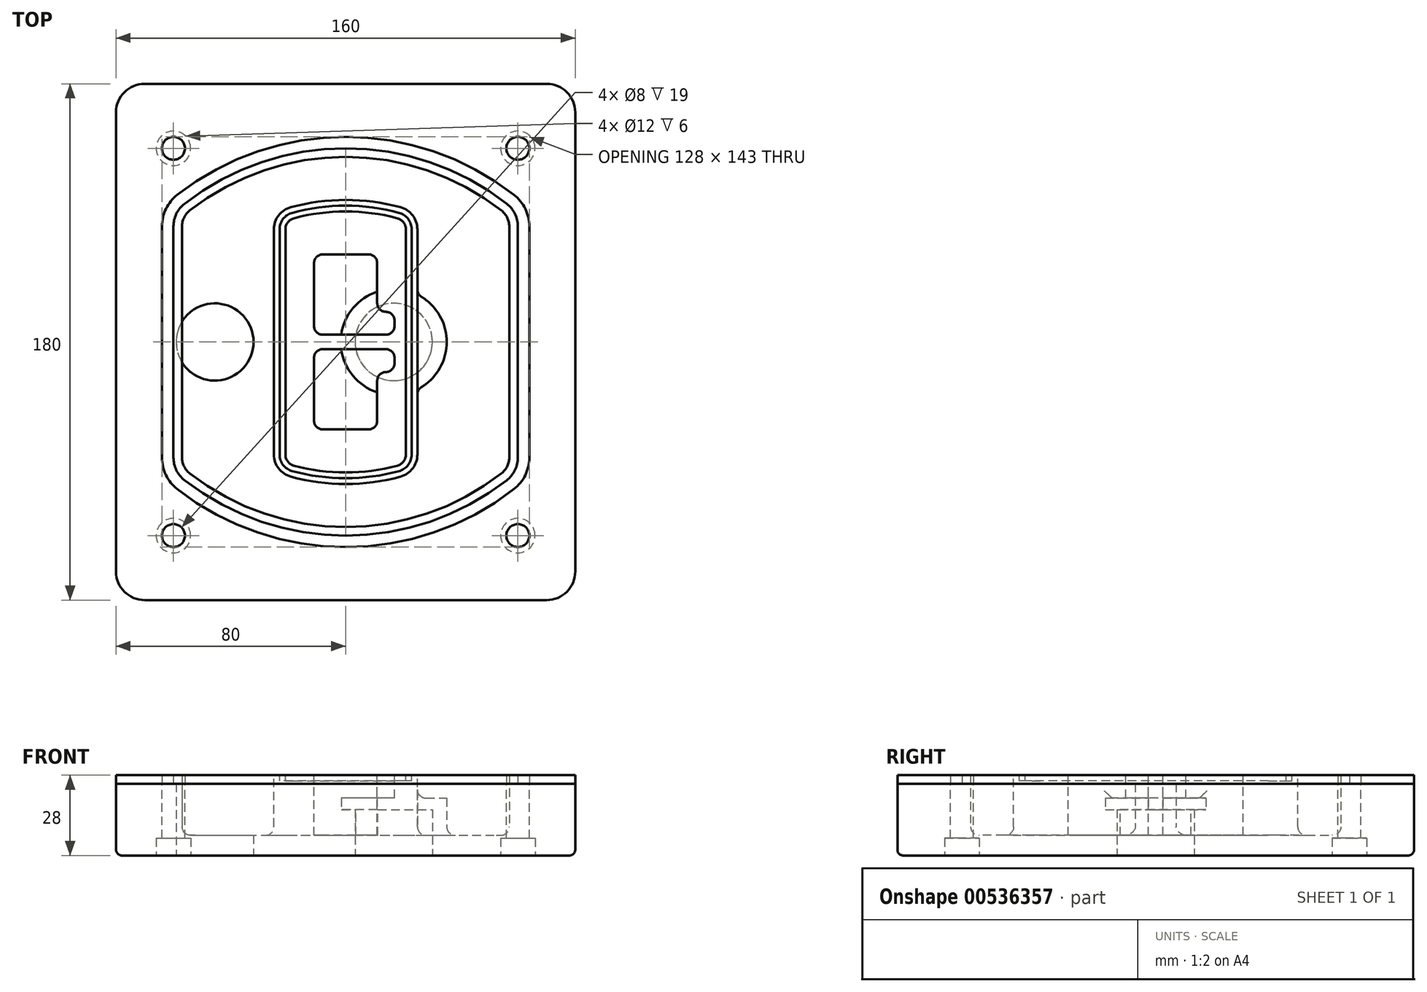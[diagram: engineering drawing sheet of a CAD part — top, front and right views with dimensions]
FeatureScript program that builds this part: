
annotation { "Feature Type Name" : "Feature", "Feature Type Description" : "" }
export const myFeature = defineFeature(function(context is Context, id is Id, definition is map)
    precondition{}
    {
        {
            var Q0;
            Q0=qCreatedBy(makeId("Top.planeOp"),FACE);
            var sketch = newSketch(context, id + "F0", { "sketchPlane" : qUnion([Q0])});
            skPoint(sketch, "E0.rect.middle", {"position": v(0, 0) * mm});
            skLineSegment(sketch, "E1.bottom", {"start": v(-70, -90) * mm, "end": v(70, -90) * mm});
            skLineSegment(sketch, "E1.top", {"start": v(-70, 90) * mm, "end": v(70, 90) * mm});
            skLineSegment(sketch, "E1.left", {"start": v(-80, -80) * mm, "end": v(-80, 80) * mm});
            skLineSegment(sketch, "E1.right", {"start": v(80, -80) * mm, "end": v(80, 80) * mm});
            skLineSegment(sketch, "E2", {"start": v(-80, 90) * mm, "end": v(80, -90) * mm, "construction": true});
            skLineSegment(sketch, "E3", {"start": v(80, 90) * mm, "end": v(-80, -90) * mm, "construction": true});
            skCircle(sketch, "E4", {"center": v(-60, 67.5) * mm, "radius": 4 * mm});
            skCircle(sketch, "E5", {"center": v(60, 67.5) * mm, "radius": 4 * mm});
            skCircle(sketch, "E6", {"center": v(60, -67.5) * mm, "radius": 4 * mm});
            skCircle(sketch, "E7", {"center": v(-60, -67.5) * mm, "radius": 4 * mm});
            skLineSegment(sketch, "E8", {"start": v(-60, 67.5) * mm, "end": v(60, 67.5) * mm, "construction": true});
            skLineSegment(sketch, "E9", {"start": v(60, 67.5) * mm, "end": v(60, -67.5) * mm, "construction": true});
            skLineSegment(sketch, "E10", {"start": v(60, -67.5) * mm, "end": v(-60, -67.5) * mm, "construction": true});
            skLineSegment(sketch, "E11", {"start": v(-60, -67.5) * mm, "end": v(-60, 67.5) * mm, "construction": true});
            skLineSegment(sketch, "E12", {"start": v(-60, 40.3) * mm, "end": v(-60, -40.3) * mm});
            skLineSegment(sketch, "E13", {"start": v(60, 40.3) * mm, "end": v(60, -40.3) * mm});
            skArc(sketch, "E14", {"start": v(56.15, 48.18) * mm, "mid": v(0, 67.5) * mm, "end": v(-56.15, 48.18) * mm});
            skArc(sketch, "E15", {"start": v(-56.15, -48.18) * mm, "mid": v(0, -67.5) * mm, "end": v(56.15, -48.18) * mm});
            skLineSegment(sketch, "E16", {"start": v(-60, 0) * mm, "end": v(60, 0) * mm, "construction": true});
            skPoint(sketch, "E17.visualSharp", {"position": v(-60, -45) * mm});
            skArc(sketch, "E17.filletArc", {"start": v(-60, -40.3) * mm, "mid": v(-58.99, -44.68) * mm, "end": v(-56.15, -48.18) * mm});
            skPoint(sketch, "E18.visualSharp", {"position": v(-60, 45) * mm});
            skArc(sketch, "E18.filletArc", {"start": v(-56.15, 48.18) * mm, "mid": v(-58.99, 44.68) * mm, "end": v(-60, 40.3) * mm});
            skPoint(sketch, "E19.visualSharp", {"position": v(60, 45) * mm});
            skArc(sketch, "E19.filletArc", {"start": v(60, 40.3) * mm, "mid": v(58.99, 44.68) * mm, "end": v(56.15, 48.18) * mm});
            skPoint(sketch, "E20.visualSharp", {"position": v(60, -45) * mm});
            skArc(sketch, "E20.filletArc", {"start": v(56.15, -48.18) * mm, "mid": v(58.99, -44.68) * mm, "end": v(60, -40.3) * mm});
            skPoint(sketch, "E21.visualSharp", {"position": v(-80, 90) * mm});
            skArc(sketch, "E21.filletArc", {"start": v(-70, 90) * mm, "mid": v(-77.07, 87.07) * mm, "end": v(-80, 80) * mm});
            skPoint(sketch, "E22.visualSharp", {"position": v(80, 90) * mm});
            skArc(sketch, "E22.filletArc", {"start": v(80, 80) * mm, "mid": v(77.07, 87.07) * mm, "end": v(70, 90) * mm});
            skPoint(sketch, "E23.visualSharp", {"position": v(80, -90) * mm});
            skArc(sketch, "E23.filletArc", {"start": v(70, -90) * mm, "mid": v(77.07, -87.07) * mm, "end": v(80, -80) * mm});
            skPoint(sketch, "E24.visualSharp", {"position": v(-80, -90) * mm});
            skArc(sketch, "E24.filletArc", {"start": v(-80, -80) * mm, "mid": v(-77.07, -87.07) * mm, "end": v(-70, -90) * mm});
            skArc(sketch, "E25.0", {"start": v(57, 40.3) * mm, "mid": v(56.3, 43.36) * mm, "end": v(54.3, 45.81) * mm});
            skLineSegment(sketch, "E25.1", {"start": v(57, 40.3) * mm, "end": v(57, -40.3) * mm});
            skArc(sketch, "E25.2", {"start": v(54.3, -45.81) * mm, "mid": v(56.3, -43.36) * mm, "end": v(57, -40.3) * mm});
            skArc(sketch, "E25.3", {"start": v(-54.3, -45.81) * mm, "mid": v(0, -64.5) * mm, "end": v(54.3, -45.81) * mm});
            skArc(sketch, "E25.4", {"start": v(-57, -40.3) * mm, "mid": v(-56.3, -43.36) * mm, "end": v(-54.3, -45.81) * mm});
            skArc(sketch, "E25.5", {"start": v(54.3, 45.81) * mm, "mid": v(0, 64.5) * mm, "end": v(-54.3, 45.81) * mm});
            skLineSegment(sketch, "E25.6", {"start": v(-57, 40.3) * mm, "end": v(-57, -40.3) * mm});
            skArc(sketch, "E25.7", {"start": v(-54.3, 45.81) * mm, "mid": v(-56.3, 43.36) * mm, "end": v(-57, 40.3) * mm});
            skArc(sketch, "E26.0", {"start": v(-58.62, 51.33) * mm, "mid": v(-62.58, 46.43) * mm, "end": v(-64, 40.3) * mm});
            skArc(sketch, "E26.1", {"start": v(58.62, 51.33) * mm, "mid": v(0, 71.5) * mm, "end": v(-58.62, 51.33) * mm});
            skArc(sketch, "E26.2", {"start": v(64, 40.3) * mm, "mid": v(62.58, 46.43) * mm, "end": v(58.62, 51.33) * mm});
            skLineSegment(sketch, "E26.3", {"start": v(64, 40.3) * mm, "end": v(64, -40.3) * mm});
            skArc(sketch, "E26.4", {"start": v(58.62, -51.33) * mm, "mid": v(62.58, -46.43) * mm, "end": v(64, -40.3) * mm});
            skLineSegment(sketch, "E26.5", {"start": v(-64, 40.3) * mm, "end": v(-64, -40.3) * mm});
            skArc(sketch, "E26.6", {"start": v(-58.62, -51.33) * mm, "mid": v(0, -71.5) * mm, "end": v(58.62, -51.33) * mm});
            skArc(sketch, "E26.7", {"start": v(-64, -40.3) * mm, "mid": v(-62.58, -46.43) * mm, "end": v(-58.62, -51.33) * mm});
            skSolve(sketch);
        }
        {
            var Q0;
            Q0=makeQuery(id+"F0.imprint","IMPRINT",FACE,{"disambiguationData":[TD([[makeQuery(id+"F0.imprint","IMPRINT",EDGE,{"derivedFrom":sQuery(id+"F0.wireOp",EDGE,"E1.bottom")}),1.0]])]});
            var Q1;
            Q1=makeQuery(id+"F0.imprint","IMPRINT",FACE,{"disambiguationData":[TD([[makeQuery(id+"F0.imprint","IMPRINT",EDGE,{"derivedFrom":sQuery(id+"F0.wireOp",EDGE,"E12")}),1.0]])]});
            var Q2;
            Q2=makeQuery(id+"F0.imprint","IMPRINT",FACE,{"disambiguationData":[TD([[makeQuery(id+"F0.imprint","IMPRINT",EDGE,{"derivedFrom":sQuery(id+"F0.wireOp",EDGE,"E25.0")}),1.0]])]});
            var Q3;
            Q3=makeQuery(id+"F0.imprint","IMPRINT",FACE,{"disambiguationData":[TD([[makeQuery(id+"F0.imprint","IMPRINT",EDGE,{"derivedFrom":sQuery(id+"F0.wireOp",EDGE,"E12")}),-1.0]])]});
            extrude(context, id + "F1", {"entities" : qUnion([Q0, Q1, Q2, Q3]), "oppositeDirection" : true, "depth" : 25 * mm});
        }
        {
            var Q0;
            Q0=makeQuery(id+"F0.imprint","IMPRINT",FACE,{"disambiguationData":[TD([[makeQuery(id+"F0.imprint","IMPRINT",EDGE,{"derivedFrom":sQuery(id+"F0.wireOp",EDGE,"E12")}),1.0]])]});
            extrude(context, id + "F2", {"entities" : qUnion([Q0]), "operationType" : NewBodyOperationType.ADD, "depth" : 3 * mm});
        }
        {
            var Q0;
            Q0=makeQuery(id+"F0.imprint","IMPRINT",FACE,{"disambiguationData":[TD([[makeQuery(id+"F0.imprint","IMPRINT",EDGE,{"derivedFrom":sQuery(id+"F0.wireOp",EDGE,"E25.0")}),1.0]])]});
            extrude(context, id + "F3", {"entities" : qUnion([Q0]), "operationType" : NewBodyOperationType.REMOVE, "oppositeDirection" : true, "depth" : 18 * mm});
        }
        {
            var Q0;
            Q0=makeQuery(id+"F2.opExtrude","CAP_FACE",FACE,{"disambiguationData":[OSD([sQuery(id+"F0.wireOp",EDGE,"E12"),sQuery(id+"F0.wireOp",EDGE,"E13"),sQuery(id+"F0.wireOp",EDGE,"E14"),sQuery(id+"F0.wireOp",EDGE,"E15"),sQuery(id+"F0.wireOp",EDGE,"E17.filletArc"),sQuery(id+"F0.wireOp",EDGE,"E18.filletArc"),sQuery(id+"F0.wireOp",EDGE,"E19.filletArc"),sQuery(id+"F0.wireOp",EDGE,"E20.filletArc"),sQuery(id+"F0.wireOp",EDGE,"E25.0"),sQuery(id+"F0.wireOp",EDGE,"E25.1"),sQuery(id+"F0.wireOp",EDGE,"E25.2"),sQuery(id+"F0.wireOp",EDGE,"E25.3"),sQuery(id+"F0.wireOp",EDGE,"E25.4"),sQuery(id+"F0.wireOp",EDGE,"E25.5"),sQuery(id+"F0.wireOp",EDGE,"E25.6"),sQuery(id+"F0.wireOp",EDGE,"E25.7")])],"isStart":false});
            var sketch = newSketch(context, id + "F4", { "sketchPlane" : qUnion([Q0])});
            skArc(sketch, "E27.0", {"start": v(-19.08, -46.97) * mm, "mid": v(0, -49.5) * mm, "end": v(19.08, -46.97) * mm});
            skArc(sketch, "E28.0", {"start": v(19.08, 46.97) * mm, "mid": v(0, 49.5) * mm, "end": v(-19.08, 46.97) * mm});
            skLineSegment(sketch, "E29", {"start": v(-25, 39.25) * mm, "end": v(-25, -39.25) * mm});
            skLineSegment(sketch, "E30", {"start": v(25, 39.25) * mm, "end": v(25, -39.25) * mm});
            skLineSegment(sketch, "E31", {"start": v(-25, 45.1) * mm, "end": v(25, 45.1) * mm, "construction": true});
            skLineSegment(sketch, "E32", {"start": v(-25, -45.1) * mm, "end": v(25, -45.1) * mm, "construction": true});
            skPoint(sketch, "E33.visualSharp", {"position": v(-25, 45.1) * mm});
            skArc(sketch, "E33.filletArc", {"start": v(-19.08, 46.97) * mm, "mid": v(-23.35, 44.11) * mm, "end": v(-25, 39.25) * mm});
            skPoint(sketch, "E34.visualSharp", {"position": v(25, 45.1) * mm});
            skArc(sketch, "E34.filletArc", {"start": v(25, 39.25) * mm, "mid": v(23.35, 44.11) * mm, "end": v(19.08, 46.97) * mm});
            skPoint(sketch, "E35.visualSharp", {"position": v(25, -45.1) * mm});
            skArc(sketch, "E35.filletArc", {"start": v(19.08, -46.97) * mm, "mid": v(23.35, -44.11) * mm, "end": v(25, -39.25) * mm});
            skPoint(sketch, "E36.visualSharp", {"position": v(-25, -45.1) * mm});
            skArc(sketch, "E36.filletArc", {"start": v(-25, -39.25) * mm, "mid": v(-23.35, -44.11) * mm, "end": v(-19.08, -46.97) * mm});
            skArc(sketch, "E37.0", {"start": v(54.3, 45.81) * mm, "mid": v(0, 64.5) * mm, "end": v(-54.3, 45.81) * mm});
            skArc(sketch, "E37.1", {"start": v(-54.3, 45.81) * mm, "mid": v(-56.3, 43.36) * mm, "end": v(-57, 40.3) * mm});
            skLineSegment(sketch, "E37.2", {"start": v(-57, 40.3) * mm, "end": v(-57, -40.3) * mm});
            skArc(sketch, "E37.3", {"start": v(-57, -40.3) * mm, "mid": v(-56.3, -43.36) * mm, "end": v(-54.3, -45.81) * mm});
            skArc(sketch, "E37.4", {"start": v(-54.3, -45.81) * mm, "mid": v(0, -64.5) * mm, "end": v(54.3, -45.81) * mm});
            skArc(sketch, "E37.5", {"start": v(54.3, -45.81) * mm, "mid": v(56.3, -43.36) * mm, "end": v(57, -40.3) * mm});
            skLineSegment(sketch, "E37.6", {"start": v(57, 40.3) * mm, "end": v(57, -40.3) * mm});
            skArc(sketch, "E37.7", {"start": v(57, 40.3) * mm, "mid": v(56.3, 43.36) * mm, "end": v(54.3, 45.81) * mm});
            skLineSegment(sketch, "E38.0", {"start": v(23, 39.25) * mm, "end": v(23, -39.25) * mm});
            skArc(sketch, "E38.1", {"start": v(18.56, -45.04) * mm, "mid": v(21.76, -42.9) * mm, "end": v(23, -39.25) * mm});
            skArc(sketch, "E38.2", {"start": v(-18.56, -45.04) * mm, "mid": v(0, -47.5) * mm, "end": v(18.56, -45.04) * mm});
            skArc(sketch, "E38.3", {"start": v(-23, -39.25) * mm, "mid": v(-21.76, -42.9) * mm, "end": v(-18.56, -45.04) * mm});
            skLineSegment(sketch, "E38.4", {"start": v(-23, 39.25) * mm, "end": v(-23, -39.25) * mm});
            skArc(sketch, "E38.5", {"start": v(23, 39.25) * mm, "mid": v(21.76, 42.9) * mm, "end": v(18.56, 45.04) * mm});
            skArc(sketch, "E38.6", {"start": v(-18.56, 45.04) * mm, "mid": v(-21.76, 42.9) * mm, "end": v(-23, 39.25) * mm});
            skArc(sketch, "E38.7", {"start": v(18.56, 45.04) * mm, "mid": v(0, 47.5) * mm, "end": v(-18.56, 45.04) * mm});
            skArc(sketch, "E39.0", {"start": v(21, 39.25) * mm, "mid": v(20.18, 41.68) * mm, "end": v(18.04, 43.1) * mm});
            skLineSegment(sketch, "E39.1", {"start": v(21, 39.25) * mm, "end": v(21, -39.25) * mm});
            skArc(sketch, "E39.2", {"start": v(18.04, -43.1) * mm, "mid": v(20.18, -41.68) * mm, "end": v(21, -39.25) * mm});
            skArc(sketch, "E39.3", {"start": v(-18.04, -43.1) * mm, "mid": v(0, -45.5) * mm, "end": v(18.04, -43.1) * mm});
            skArc(sketch, "E39.4", {"start": v(-21, -39.25) * mm, "mid": v(-20.18, -41.68) * mm, "end": v(-18.04, -43.1) * mm});
            skArc(sketch, "E39.5", {"start": v(18.04, 43.1) * mm, "mid": v(0, 45.5) * mm, "end": v(-18.04, 43.1) * mm});
            skLineSegment(sketch, "E39.6", {"start": v(-21, 39.25) * mm, "end": v(-21, -39.25) * mm});
            skArc(sketch, "E39.7", {"start": v(-18.04, 43.1) * mm, "mid": v(-20.18, 41.68) * mm, "end": v(-21, 39.25) * mm});
            skLineSegment(sketch, "E40", {"start": v(-25, 0) * mm, "end": v(25, 0) * mm, "construction": true});
            skLineSegment(sketch, "E41", {"start": v(-11, 5.5) * mm, "end": v(-11, 27.5) * mm});
            skLineSegment(sketch, "E42", {"start": v(-8, 30.5) * mm, "end": v(8, 30.5) * mm});
            skLineSegment(sketch, "E43", {"start": v(11, 27.5) * mm, "end": v(11, 13.5) * mm});
            skLineSegment(sketch, "E44", {"start": v(14, 10.5) * mm, "end": v(14, 10.5) * mm});
            skLineSegment(sketch, "E45", {"start": v(17, 7.5) * mm, "end": v(17, 5.5) * mm});
            skLineSegment(sketch, "E46", {"start": v(14, 2.5) * mm, "end": v(-8, 2.5) * mm});
            skPoint(sketch, "E47.visualSharp", {"position": v(-11, 30.5) * mm});
            skArc(sketch, "E47.filletArc", {"start": v(-8, 30.5) * mm, "mid": v(-10.12, 29.62) * mm, "end": v(-11, 27.5) * mm});
            skPoint(sketch, "E48.visualSharp", {"position": v(11, 30.5) * mm});
            skArc(sketch, "E48.filletArc", {"start": v(11, 27.5) * mm, "mid": v(10.12, 29.62) * mm, "end": v(8, 30.5) * mm});
            skPoint(sketch, "E49.visualSharp", {"position": v(11, 10.5) * mm});
            skArc(sketch, "E49.filletArc", {"start": v(11, 13.5) * mm, "mid": v(11.88, 11.38) * mm, "end": v(14, 10.5) * mm});
            skPoint(sketch, "E50.visualSharp", {"position": v(17, 10.5) * mm});
            skArc(sketch, "E50.filletArc", {"start": v(17, 7.5) * mm, "mid": v(16.12, 9.62) * mm, "end": v(14, 10.5) * mm});
            skPoint(sketch, "E51.visualSharp", {"position": v(17, 2.5) * mm});
            skArc(sketch, "E51.filletArc", {"start": v(14, 2.5) * mm, "mid": v(16.12, 3.38) * mm, "end": v(17, 5.5) * mm});
            skPoint(sketch, "E52.visualSharp", {"position": v(-11, 2.5) * mm});
            skArc(sketch, "E52.filletArc", {"start": v(-11, 5.5) * mm, "mid": v(-10.12, 3.38) * mm, "end": v(-8, 2.5) * mm});
            skLineSegment(sketch, "E53.0.MirrorCS", {"start": v(14, -2.5) * mm, "end": v(-8, -2.5) * mm});
            skArc(sketch, "E54.0.MirrorCS", {"start": v(-11, -5.5) * mm, "mid": v(-10.12, -3.38) * mm, "end": v(-8, -2.5) * mm});
            skLineSegment(sketch, "E55.0.MirrorCS", {"start": v(-11, -5.5) * mm, "end": v(-11, -27.5) * mm});
            skArc(sketch, "E56.0.MirrorCS", {"start": v(-8, -30.5) * mm, "mid": v(-10.12, -29.62) * mm, "end": v(-11, -27.5) * mm});
            skLineSegment(sketch, "E57.0.MirrorCS", {"start": v(-8, -30.5) * mm, "end": v(8, -30.5) * mm});
            skArc(sketch, "E58.0.MirrorCS", {"start": v(11, -27.5) * mm, "mid": v(10.12, -29.62) * mm, "end": v(8, -30.5) * mm});
            skLineSegment(sketch, "E59.0.MirrorCS", {"start": v(11, -27.5) * mm, "end": v(11, -13.5) * mm});
            skArc(sketch, "E60.0.MirrorCS", {"start": v(11, -13.5) * mm, "mid": v(11.88, -11.38) * mm, "end": v(14, -10.5) * mm});
            skArc(sketch, "E61.0.MirrorCS", {"start": v(17, -7.5) * mm, "mid": v(16.12, -9.62) * mm, "end": v(14, -10.5) * mm});
            skLineSegment(sketch, "E62.0.MirrorCS", {"start": v(17, -7.5) * mm, "end": v(17, -5.5) * mm});
            skArc(sketch, "E63.0.MirrorCS", {"start": v(14, -2.5) * mm, "mid": v(16.12, -3.38) * mm, "end": v(17, -5.5) * mm});
            skSolve(sketch);
        }
        {
            var Q0;
            Q0=makeQuery(id+"F4.imprint","IMPRINT",FACE,{"disambiguationData":[TD([[makeQuery(id+"F4.imprint","IMPRINT",EDGE,{"derivedFrom":sQuery(id+"F4.wireOp",EDGE,"E27.0")}),1.0]])]});
            var Q1;
            Q1=makeQuery(id+"F4.imprint","IMPRINT",FACE,{"disambiguationData":[TD([[makeQuery(id+"F4.imprint","IMPRINT",EDGE,{"derivedFrom":sQuery(id+"F4.wireOp",EDGE,"E38.0")}),-1.0]])]});
            var Q2;
            Q2=makeQuery(id+"F4.imprint","IMPRINT",FACE,{"disambiguationData":[TD([[makeQuery(id+"F4.imprint","IMPRINT",EDGE,{"derivedFrom":sQuery(id+"F4.wireOp",EDGE,"E39.0")}),1.0]])]});
            extrude(context, id + "F5", {"entities" : qUnion([Q0, Q1, Q2]), "operationType" : NewBodyOperationType.ADD, "endBound" : BoundingType.UP_TO_NEXT, "oppositeDirection" : true, "depth" : 25 * mm});
        }
        {
            var Q0;
            Q0=makeQuery(id+"F4.imprint","IMPRINT",FACE,{"disambiguationData":[TD([[makeQuery(id+"F4.imprint","IMPRINT",EDGE,{"derivedFrom":sQuery(id+"F4.wireOp",EDGE,"E38.0")}),-1.0]])]});
            extrude(context, id + "F6", {"entities" : qUnion([Q0]), "operationType" : NewBodyOperationType.REMOVE, "oppositeDirection" : true, "depth" : 2 * mm});
        }
        {
            var Q0;
            Q0=makeQuery(id+"F1.opExtrude","CAP_FACE",FACE,{"disambiguationData":[OSD([sQuery(id+"F0.wireOp",EDGE,"E1.bottom"),sQuery(id+"F0.wireOp",EDGE,"E1.top"),sQuery(id+"F0.wireOp",EDGE,"E1.left"),sQuery(id+"F0.wireOp",EDGE,"E1.right"),sQuery(id+"F0.wireOp",EDGE,"E4"),sQuery(id+"F0.wireOp",EDGE,"E5"),sQuery(id+"F0.wireOp",EDGE,"E6"),sQuery(id+"F0.wireOp",EDGE,"E7"),sQuery(id+"F0.wireOp",EDGE,"E21.filletArc"),sQuery(id+"F0.wireOp",EDGE,"E22.filletArc"),sQuery(id+"F0.wireOp",EDGE,"E23.filletArc"),sQuery(id+"F0.wireOp",EDGE,"E24.filletArc")])],"isStart":false});
            var sketch = newSketch(context, id + "F7", { "sketchPlane" : qUnion([Q0])});
            skCircle(sketch, "E64", {"center": v(16.76, 0) * mm, "radius": 13.47 * mm});
            skCircle(sketch, "E65", {"center": v(-45.56, 0) * mm, "radius": 13.47 * mm});
            skLineSegment(sketch, "E66", {"start": v(80, 0) * mm, "end": v(-80, 0) * mm});
            skCircle(sketch, "E67", {"center": v(16.76, 0) * mm, "radius": 18.47 * mm});
            skCircle(sketch, "E68", {"center": v(60, -67.5) * mm, "radius": 6 * mm});
            skCircle(sketch, "E69", {"center": v(-60, -67.5) * mm, "radius": 6 * mm});
            skCircle(sketch, "E70", {"center": v(-60, 67.5) * mm, "radius": 6 * mm});
            skCircle(sketch, "E71", {"center": v(60, 67.5) * mm, "radius": 6 * mm});
            skSolve(sketch);
        }
        {
            var Q0;
            {var subQ1=sQuery(id+"F7.wireOp",EDGE,"E66");var subQ4=sQuery(id+"F7.wireOp",EDGE,"E64");var subQ6=makeQuery(id+"F7.imprint","INTERSECT",VERTEX,{"disambiguationData":[OD(0.0)],"derivedFrom":[subQ4,subQ1]});Q0=makeQuery(id+"F7.imprint","IMPRINT",FACE,{"disambiguationData":[TD([[makeQuery(id+"F7.imprint","IMPRINT",EDGE,{"disambiguationData":[TD([[subQ6,-1.0]])],"derivedFrom":subQ4}),-1.0]])]});}
            var Q1;
            {var subQ0=sQuery(id+"F7.wireOp",EDGE,"E66");var subQ1=sQuery(id+"F7.wireOp",EDGE,"E64");var subQ3=makeQuery(id+"F7.imprint","INTERSECT",VERTEX,{"disambiguationData":[OD(0.0)],"derivedFrom":[subQ1,subQ0]});Q1=makeQuery(id+"F7.imprint","IMPRINT",FACE,{"disambiguationData":[TD([[makeQuery(id+"F7.imprint","IMPRINT",EDGE,{"disambiguationData":[TD([[subQ3,-1.0]])],"derivedFrom":subQ1}),1.0]])]});}
            var Q2;
            {var subQ0=sQuery(id+"F7.wireOp",EDGE,"E66");var subQ1=sQuery(id+"F7.wireOp",EDGE,"E64");var subQ3=makeQuery(id+"F7.imprint","INTERSECT",VERTEX,{"disambiguationData":[OD(0.0)],"derivedFrom":[subQ1,subQ0]});Q2=makeQuery(id+"F7.imprint","IMPRINT",FACE,{"disambiguationData":[TD([[makeQuery(id+"F7.imprint","IMPRINT",EDGE,{"disambiguationData":[TD([[subQ3,1.0]])],"derivedFrom":subQ1}),1.0]])]});}
            var Q3;
            {var subQ1=sQuery(id+"F7.wireOp",EDGE,"E66");var subQ4=sQuery(id+"F7.wireOp",EDGE,"E64");var subQ6=makeQuery(id+"F7.imprint","INTERSECT",VERTEX,{"disambiguationData":[OD(0.0)],"derivedFrom":[subQ4,subQ1]});Q3=makeQuery(id+"F7.imprint","IMPRINT",FACE,{"disambiguationData":[TD([[makeQuery(id+"F7.imprint","IMPRINT",EDGE,{"disambiguationData":[TD([[subQ6,1.0]])],"derivedFrom":subQ4}),-1.0]])]});}
            extrude(context, id + "F8", {"entities" : qUnion([Q0, Q1, Q2, Q3]), "operationType" : NewBodyOperationType.ADD, "oppositeDirection" : true, "depth" : 20 * mm});
        }
        {
            var Q0;
            {var subQ0=sQuery(id+"F7.wireOp",EDGE,"E66");var subQ1=sQuery(id+"F7.wireOp",EDGE,"E64");var subQ3=makeQuery(id+"F7.imprint","INTERSECT",VERTEX,{"disambiguationData":[OD(0.0)],"derivedFrom":[subQ1,subQ0]});Q0=makeQuery(id+"F7.imprint","IMPRINT",FACE,{"disambiguationData":[TD([[makeQuery(id+"F7.imprint","IMPRINT",EDGE,{"disambiguationData":[TD([[subQ3,-1.0]])],"derivedFrom":subQ1}),1.0]])]});}
            var Q1;
            {var subQ0=sQuery(id+"F7.wireOp",EDGE,"E66");var subQ1=sQuery(id+"F7.wireOp",EDGE,"E64");var subQ3=makeQuery(id+"F7.imprint","INTERSECT",VERTEX,{"disambiguationData":[OD(0.0)],"derivedFrom":[subQ1,subQ0]});Q1=makeQuery(id+"F7.imprint","IMPRINT",FACE,{"disambiguationData":[TD([[makeQuery(id+"F7.imprint","IMPRINT",EDGE,{"disambiguationData":[TD([[subQ3,1.0]])],"derivedFrom":subQ1}),1.0]])]});}
            extrude(context, id + "F9", {"entities" : qUnion([Q0, Q1]), "operationType" : NewBodyOperationType.REMOVE, "oppositeDirection" : true, "depth" : 16 * mm});
        }
        {
            var Q0;
            {var subQ0=sQuery(id+"F7.wireOp",EDGE,"E66");var subQ1=sQuery(id+"F7.wireOp",EDGE,"E65");var subQ3=makeQuery(id+"F7.imprint","INTERSECT",VERTEX,{"disambiguationData":[OD(0.0)],"derivedFrom":[subQ1,subQ0]});Q0=makeQuery(id+"F7.imprint","IMPRINT",FACE,{"disambiguationData":[TD([[makeQuery(id+"F7.imprint","IMPRINT",EDGE,{"disambiguationData":[TD([[subQ3,-1.0]])],"derivedFrom":subQ1}),1.0]])]});}
            var Q1;
            {var subQ0=sQuery(id+"F7.wireOp",EDGE,"E66");var subQ1=sQuery(id+"F7.wireOp",EDGE,"E65");var subQ3=makeQuery(id+"F7.imprint","INTERSECT",VERTEX,{"disambiguationData":[OD(0.0)],"derivedFrom":[subQ1,subQ0]});Q1=makeQuery(id+"F7.imprint","IMPRINT",FACE,{"disambiguationData":[TD([[makeQuery(id+"F7.imprint","IMPRINT",EDGE,{"disambiguationData":[TD([[subQ3,1.0]])],"derivedFrom":subQ1}),1.0]])]});}
            extrude(context, id + "F10", {"entities" : qUnion([Q0, Q1]), "operationType" : NewBodyOperationType.REMOVE, "oppositeDirection" : true, "depth" : 25 * mm});
        }
        {
            var Q0;
            Q0=makeQuery(id+"F7.imprint","IMPRINT",FACE,{"disambiguationData":[TD([[makeQuery(id+"F7.imprint","IMPRINT",EDGE,{"derivedFrom":sQuery(id+"F7.wireOp",EDGE,"E68")}),1.0]])]});
            var Q1;
            Q1=makeQuery(id+"F7.imprint","IMPRINT",FACE,{"disambiguationData":[TD([[makeQuery(id+"F7.imprint","IMPRINT",EDGE,{"derivedFrom":makeQuery(id+"F1.opExtrude","CAP_EDGE",EDGE,{"disambiguationData":[OSD([sQuery(id+"F0.wireOp",EDGE,"E5")])],"isStart":false})}),-1.0]])]});
            var Q2;
            Q2=makeQuery(id+"F7.imprint","IMPRINT",FACE,{"disambiguationData":[TD([[makeQuery(id+"F7.imprint","IMPRINT",EDGE,{"derivedFrom":sQuery(id+"F7.wireOp",EDGE,"E69")}),1.0]])]});
            var Q3;
            Q3=makeQuery(id+"F7.imprint","IMPRINT",FACE,{"disambiguationData":[TD([[makeQuery(id+"F7.imprint","IMPRINT",EDGE,{"derivedFrom":makeQuery(id+"F1.opExtrude","CAP_EDGE",EDGE,{"disambiguationData":[OSD([sQuery(id+"F0.wireOp",EDGE,"E4")])],"isStart":false})}),-1.0]])]});
            var Q4;
            Q4=makeQuery(id+"F7.imprint","IMPRINT",FACE,{"disambiguationData":[TD([[makeQuery(id+"F7.imprint","IMPRINT",EDGE,{"derivedFrom":sQuery(id+"F7.wireOp",EDGE,"E70")}),1.0]])]});
            var Q5;
            Q5=makeQuery(id+"F7.imprint","IMPRINT",FACE,{"disambiguationData":[TD([[makeQuery(id+"F7.imprint","IMPRINT",EDGE,{"derivedFrom":makeQuery(id+"F1.opExtrude","CAP_EDGE",EDGE,{"disambiguationData":[OSD([sQuery(id+"F0.wireOp",EDGE,"E7")])],"isStart":false})}),-1.0]])]});
            var Q6;
            Q6=makeQuery(id+"F7.imprint","IMPRINT",FACE,{"disambiguationData":[TD([[makeQuery(id+"F7.imprint","IMPRINT",EDGE,{"derivedFrom":sQuery(id+"F7.wireOp",EDGE,"E71")}),1.0]])]});
            var Q7;
            Q7=makeQuery(id+"F7.imprint","IMPRINT",FACE,{"disambiguationData":[TD([[makeQuery(id+"F7.imprint","IMPRINT",EDGE,{"derivedFrom":makeQuery(id+"F1.opExtrude","CAP_EDGE",EDGE,{"disambiguationData":[OSD([sQuery(id+"F0.wireOp",EDGE,"E6")])],"isStart":false})}),-1.0]])]});
            extrude(context, id + "F11", {"entities" : qUnion([Q0, Q1, Q2, Q3, Q4, Q5, Q6, Q7]), "operationType" : NewBodyOperationType.REMOVE, "oppositeDirection" : true, "depth" : 6 * mm});
        }
        {
            var Q0;
            Q0=makeQuery(id+"F9.boolean.opBoolean","COPY",FACE,{"derivedFrom":makeQuery(id+"F9.opExtrude","CAP_FACE",FACE,{"disambiguationData":[OSD([sQuery(id+"F7.wireOp",EDGE,"E64")])],"isStart":false})});
            var sketch = newSketch(context, id + "F12", { "sketchPlane" : qUnion([Q0])});
            skArc(sketch, "E72.0", {"start": v(11, 17.55) * mm, "mid": v(2.57, 11.82) * mm, "end": v(-1.54, 2.5) * mm});
            skArc(sketch, "E72.1", {"start": v(-1.54, -2.5) * mm, "mid": v(2.57, -11.82) * mm, "end": v(11, -17.55) * mm});
            skLineSegment(sketch, "E73", {"start": v(-1.54, -2.5) * mm, "end": v(14, -2.5) * mm});
            skLineSegment(sketch, "E74.0", {"start": v(14, 2.5) * mm, "end": v(-1.54, 2.5) * mm});
            skArc(sketch, "E74.1", {"start": v(14, 2.5) * mm, "mid": v(16.12, 3.38) * mm, "end": v(17, 5.5) * mm});
            skLineSegment(sketch, "E74.2", {"start": v(17, 7.5) * mm, "end": v(17, 5.5) * mm});
            skArc(sketch, "E74.3", {"start": v(17, 7.5) * mm, "mid": v(16.12, 9.62) * mm, "end": v(14, 10.5) * mm});
            skArc(sketch, "E74.4", {"start": v(11, 13.5) * mm, "mid": v(11.88, 11.38) * mm, "end": v(14, 10.5) * mm});
            skLineSegment(sketch, "E74.5", {"start": v(11, 17.55) * mm, "end": v(11, 13.5) * mm});
            skLineSegment(sketch, "E74.7", {"start": v(14, -2.5) * mm, "end": v(-1.54, -2.5) * mm});
            skArc(sketch, "E74.8", {"start": v(14, -2.5) * mm, "mid": v(16.12, -3.38) * mm, "end": v(17, -5.5) * mm});
            skLineSegment(sketch, "E74.9", {"start": v(17, -7.5) * mm, "end": v(17, -5.5) * mm});
            skArc(sketch, "E74.10", {"start": v(17, -7.5) * mm, "mid": v(16.12, -9.62) * mm, "end": v(14, -10.5) * mm});
            skArc(sketch, "E74.11", {"start": v(11, -13.5) * mm, "mid": v(11.88, -11.38) * mm, "end": v(14, -10.5) * mm});
            skLineSegment(sketch, "E74.12", {"start": v(11, -17.55) * mm, "end": v(11, -13.5) * mm});
            skPoint(sketch, "E75.orphan", {"position": v(11, -27.5) * mm});
            skPoint(sketch, "E76.orphan", {"position": v(-8, -2.5) * mm});
            skPoint(sketch, "E77.orphan", {"position": v(-8, 2.5) * mm});
            skPoint(sketch, "E78.orphan", {"position": v(11, 27.5) * mm});
            skSolve(sketch);
        }
        {
            var Q0;
            {var subQ7=sQuery(id+"F12.wireOp",EDGE,"E72.0");var subQ14=sQuery(id+"F12.wireOp",EDGE,"E72.1");var subQ16=sQuery(id+"F12.wireOp",EDGE,"E74.1");var subQ18=sQuery(id+"F12.wireOp",EDGE,"E74.8");Q0=qUnion([makeQuery(id+"F12.imprint","IMPRINT",FACE,{"disambiguationData":[TD([[makeQuery(id+"F12.imprint","IMPRINT",EDGE,{"derivedFrom":subQ7}),1.0]])]}),makeQuery(id+"F12.imprint","IMPRINT",FACE,{"disambiguationData":[TD([[makeQuery(id+"F12.imprint","IMPRINT",EDGE,{"derivedFrom":subQ14}),1.0]])]}),makeQuery(id+"F12.imprint","IMPRINT",FACE,{"disambiguationData":[TD([[makeQuery(id+"F12.imprint","IMPRINT",EDGE,{"derivedFrom":subQ16}),1.0]])]}),makeQuery(id+"F12.imprint","IMPRINT",FACE,{"disambiguationData":[TD([[makeQuery(id+"F12.imprint","IMPRINT",EDGE,{"derivedFrom":subQ18}),-1.0]])]})]);}
            var Q1;
            Q1=makeQuery(id+"F5.boolean.opBoolean","SPLIT",FACE,{"disambiguationData":[TD([makeQuery(id+"F5.opExtrude","SWEPT_FACE",FACE,{"disambiguationData":[OSD([sQuery(id+"F4.wireOp",EDGE,"E41")])]})])],"derivedFrom":makeQuery(id+"F3.boolean.opBoolean","COPY",FACE,{"derivedFrom":makeQuery(id+"F3.opExtrude","CAP_FACE",FACE,{"disambiguationData":[OSD([sQuery(id+"F0.wireOp",EDGE,"E25.0"),sQuery(id+"F0.wireOp",EDGE,"E25.1"),sQuery(id+"F0.wireOp",EDGE,"E25.2"),sQuery(id+"F0.wireOp",EDGE,"E25.3"),sQuery(id+"F0.wireOp",EDGE,"E25.4"),sQuery(id+"F0.wireOp",EDGE,"E25.5"),sQuery(id+"F0.wireOp",EDGE,"E25.6"),sQuery(id+"F0.wireOp",EDGE,"E25.7")])],"isStart":false})})});
            extrude(context, id + "F13", {"entities" : qUnion([Q0]), "operationType" : NewBodyOperationType.REMOVE, "endBound" : BoundingType.UP_TO_SURFACE, "endBoundEntityFace" : qUnion([Q1]), "depth" : 25 * mm});
        }
        {
            var Q0;
            Q0=makeQuery(id+"F3.boolean.opBoolean","COPY",EDGE,{"derivedFrom":makeQuery(id+"F3.opExtrude","CAP_EDGE",EDGE,{"disambiguationData":[OSD([sQuery(id+"F0.wireOp",EDGE,"E25.6")])],"isStart":false})});
            var Q1;
            Q1=makeQuery(id+"F8.boolean.opBoolean","INTERSECT",EDGE,{"derivedFrom":[makeQuery(id+"F5.opExtrude","SWEPT_FACE",FACE,{"disambiguationData":[OSD([sQuery(id+"F4.wireOp",EDGE,"E30")])]}),makeQuery(id+"F8.opExtrude","CAP_FACE",FACE,{"disambiguationData":[OSD([sQuery(id+"F7.wireOp",EDGE,"E67")])],"isStart":false})]});
            var Q2;
            Q2=makeQuery(id+"F8.boolean.opBoolean","INTERSECT",EDGE,{"disambiguationData":[OD(1.0)],"derivedFrom":[makeQuery(id+"F5.opExtrude","SWEPT_FACE",FACE,{"disambiguationData":[OSD([sQuery(id+"F4.wireOp",EDGE,"E30")])]}),makeQuery(id+"F8.opExtrude","SWEPT_FACE",FACE,{"disambiguationData":[OSD([sQuery(id+"F7.wireOp",EDGE,"E67")])]})]});
            var Q3;
            {var subQ0=sQuery(id+"F4.wireOp",EDGE,"E30");Q3=makeQuery(id+"F8.boolean.opBoolean","SPLIT",EDGE,{"disambiguationData":[TD([makeQuery(id+"F5.opExtrude","SWEPT_FACE",FACE,{"disambiguationData":[OSD([sQuery(id+"F4.wireOp",EDGE,"E35.filletArc")])]})])],"derivedFrom":makeQuery(id+"F5.opExtrude","CAP_EDGE",EDGE,{"disambiguationData":[OSD([subQ0])],"isStart":false})});}
            var Q4;
            {var subQ0=sQuery(id+"F0.wireOp",EDGE,"E25.7");var subQ1=sQuery(id+"F0.wireOp",EDGE,"E25.1");var subQ2=sQuery(id+"F0.wireOp",EDGE,"E25.6");var subQ3=sQuery(id+"F0.wireOp",EDGE,"E25.5");var subQ4=sQuery(id+"F0.wireOp",EDGE,"E25.4");var subQ5=sQuery(id+"F0.wireOp",EDGE,"E25.0");var subQ6=sQuery(id+"F0.wireOp",EDGE,"E25.2");var subQ7=sQuery(id+"F0.wireOp",EDGE,"E25.3");Q4=makeQuery(id+"F8.boolean.opBoolean","INTERSECT",EDGE,{"derivedFrom":[makeQuery(id+"F5.boolean.opBoolean","SPLIT",FACE,{"disambiguationData":[TD([makeQuery(id+"F2.opExtrude","SWEPT_FACE",FACE,{"disambiguationData":[OSD([subQ5])]})])],"derivedFrom":makeQuery(id+"F3.boolean.opBoolean","COPY",FACE,{"derivedFrom":makeQuery(id+"F3.opExtrude","CAP_FACE",FACE,{"disambiguationData":[OSD([subQ5,subQ1,subQ6,subQ7,subQ4,subQ3,subQ2,subQ0])],"isStart":false})})}),makeQuery(id+"F8.opExtrude","SWEPT_FACE",FACE,{"disambiguationData":[OSD([sQuery(id+"F7.wireOp",EDGE,"E67")])]})]});}
            var Q5;
            Q5=makeQuery(id+"F8.boolean.opBoolean","INTERSECT",EDGE,{"disambiguationData":[OD(0.0)],"derivedFrom":[makeQuery(id+"F5.opExtrude","SWEPT_FACE",FACE,{"disambiguationData":[OSD([sQuery(id+"F4.wireOp",EDGE,"E30")])]}),makeQuery(id+"F8.opExtrude","SWEPT_FACE",FACE,{"disambiguationData":[OSD([sQuery(id+"F7.wireOp",EDGE,"E67")])]})]});
            fillet(context, id + "F14", {"entities" : qUnion([Q0, Q1, Q2, Q3, Q4, Q5]), "radius" : 3 * mm, "tangentPropagation" : true, "allowEdgeOverflow" : false});
        }
        {
            var Q0;
            Q0=makeQuery(id+"F1.opExtrude","CAP_EDGE",EDGE,{"disambiguationData":[OSD([sQuery(id+"F0.wireOp",EDGE,"E1.bottom")])],"isStart":false});
            fillet(context, id + "F15", {"entities" : qUnion([Q0]), "radius" : 2 * mm, "tangentPropagation" : true, "allowEdgeOverflow" : false});
        }
        {
            var Q0;
            {var subQ0=sQuery(id+"F0.wireOp",EDGE,"E21.filletArc");var subQ1=sQuery(id+"F0.wireOp",EDGE,"E7");var subQ2=sQuery(id+"F0.wireOp",EDGE,"E6");var subQ3=sQuery(id+"F0.wireOp",EDGE,"E5");var subQ4=sQuery(id+"F0.wireOp",EDGE,"E4");var subQ5=sQuery(id+"F0.wireOp",EDGE,"E22.filletArc");var subQ6=sQuery(id+"F0.wireOp",EDGE,"E1.bottom");var subQ7=sQuery(id+"F0.wireOp",EDGE,"E1.right");var subQ8=sQuery(id+"F0.wireOp",EDGE,"E1.top");var subQ9=sQuery(id+"F0.wireOp",EDGE,"E1.left");var subQ10=sQuery(id+"F0.wireOp",EDGE,"E23.filletArc");var subQ11=sQuery(id+"F0.wireOp",EDGE,"E24.filletArc");Q0=makeQuery(id+"F2.boolean.opBoolean","SPLIT",FACE,{"disambiguationData":[TD([makeQuery(id+"F1.opExtrude","SWEPT_FACE",FACE,{"disambiguationData":[OSD([subQ6])]})])],"derivedFrom":makeQuery(id+"F1.opExtrude","CAP_FACE",FACE,{"disambiguationData":[OSD([subQ6,subQ8,subQ9,subQ7,subQ4,subQ3,subQ2,subQ1,subQ0,subQ5,subQ10,subQ11])],"isStart":true})});}
            var sketch = newSketch(context, id + "F16", { "sketchPlane" : qUnion([Q0])});
            skLineSegment(sketch, "E79.0", {"start": v(-70, 90) * mm, "end": v(70, 90) * mm});
            skArc(sketch, "E80.0", {"start": v(-70, 90) * mm, "mid": v(-77.07, 87.07) * mm, "end": v(-80, 80) * mm});
            skLineSegment(sketch, "E81.0", {"start": v(-80, -80) * mm, "end": v(-80, 80) * mm});
            skArc(sketch, "E82.0", {"start": v(-80, -80) * mm, "mid": v(-77.07, -87.07) * mm, "end": v(-70, -90) * mm});
            skLineSegment(sketch, "E83.0", {"start": v(-70, -90) * mm, "end": v(70, -90) * mm});
            skArc(sketch, "E84.0", {"start": v(70, -90) * mm, "mid": v(77.07, -87.07) * mm, "end": v(80, -80) * mm});
            skLineSegment(sketch, "E85.0", {"start": v(80, -80) * mm, "end": v(80, 80) * mm});
            skArc(sketch, "E86.0", {"start": v(80, 80) * mm, "mid": v(77.07, 87.07) * mm, "end": v(70, 90) * mm});
            skCircle(sketch, "E87.0", {"center": v(60, 67.5) * mm, "radius": 4 * mm});
            skCircle(sketch, "E88.0", {"center": v(-60, 67.5) * mm, "radius": 4 * mm});
            skCircle(sketch, "E89.0", {"center": v(-60, -67.5) * mm, "radius": 4 * mm});
            skCircle(sketch, "E90.0", {"center": v(60, -67.5) * mm, "radius": 4 * mm});
            skArc(sketch, "E91.0", {"start": v(56.15, 48.18) * mm, "mid": v(0, 67.5) * mm, "end": v(-56.15, 48.18) * mm});
            skArc(sketch, "E92.0", {"start": v(60, 40.3) * mm, "mid": v(58.99, 44.68) * mm, "end": v(56.15, 48.18) * mm});
            skLineSegment(sketch, "E93.0", {"start": v(60, 40.3) * mm, "end": v(60, -40.3) * mm});
            skArc(sketch, "E94.0", {"start": v(56.15, -48.18) * mm, "mid": v(58.99, -44.68) * mm, "end": v(60, -40.3) * mm});
            skArc(sketch, "E95.0", {"start": v(-56.15, -48.18) * mm, "mid": v(0, -67.5) * mm, "end": v(56.15, -48.18) * mm});
            skArc(sketch, "E96.0", {"start": v(-60, -40.3) * mm, "mid": v(-58.99, -44.68) * mm, "end": v(-56.15, -48.18) * mm});
            skLineSegment(sketch, "E97.0", {"start": v(-60, 40.3) * mm, "end": v(-60, -40.3) * mm});
            skArc(sketch, "E98.0", {"start": v(-56.15, 48.18) * mm, "mid": v(-58.99, 44.68) * mm, "end": v(-60, 40.3) * mm});
            skLineSegment(sketch, "E99", {"start": v(0, 90) * mm, "end": v(0, 120) * mm, "construction": true});
            skPoint(sketch, "E99.endSnap0", {"position": v(0, 90) * mm});
            skCircle(sketch, "E100", {"center": v(0, 120) * mm, "radius": 6 * mm});
            skArc(sketch, "E101", {"start": v(15, 120) * mm, "mid": v(0, 135) * mm, "end": v(-15, 120) * mm});
            skLineSegment(sketch, "E102", {"start": v(-15, 120) * mm, "end": v(-15, 108) * mm});
            skLineSegment(sketch, "E103", {"start": v(15, 120) * mm, "end": v(15, 108) * mm});
            skLineSegment(sketch, "E104", {"start": v(-15, 108) * mm, "end": v(-33, 90) * mm});
            skLineSegment(sketch, "E105", {"start": v(15, 108) * mm, "end": v(33, 90) * mm});
            skLineSegment(sketch, "E106", {"start": v(-80, 0) * mm, "end": v(0, 0) * mm, "construction": true});
            skLineSegment(sketch, "E107", {"start": v(0, 0) * mm, "end": v(80, 0) * mm, "construction": true});
            skLineSegment(sketch, "E108.MirrorCS", {"start": v(-15, -108) * mm, "end": v(-33, -90) * mm});
            skLineSegment(sketch, "E109.MirrorCS", {"start": v(-15, -120) * mm, "end": v(-15, -108) * mm});
            skArc(sketch, "E110.MirrorCS", {"start": v(15, -120) * mm, "mid": v(0, -135) * mm, "end": v(-15, -120) * mm});
            skCircle(sketch, "E111.MirrorC", {"center": v(0, -120) * mm, "radius": 6 * mm});
            skLineSegment(sketch, "E112.MirrorCS", {"start": v(15, -120) * mm, "end": v(15, -108) * mm});
            skLineSegment(sketch, "E113.MirrorCS", {"start": v(15, -108) * mm, "end": v(33, -90) * mm});
            skLineSegment(sketch, "E114.MirrorCS", {"start": v(0, -90) * mm, "end": v(0, -120) * mm, "construction": true});
            skSolve(sketch);
        }
        {
            var Q0;
            Q0 = qSketchRegion(id + "F16", true);
            var Q1;
            Q1 = qSketchRegion(id + "F0", true);
            var Q2;
            Q2=makeQuery(id+"F2.opExtrude","CAP_FACE",FACE,{"disambiguationData":[OSD([sQuery(id+"F0.wireOp",EDGE,"E12"),sQuery(id+"F0.wireOp",EDGE,"E13"),sQuery(id+"F0.wireOp",EDGE,"E14"),sQuery(id+"F0.wireOp",EDGE,"E15"),sQuery(id+"F0.wireOp",EDGE,"E17.filletArc"),sQuery(id+"F0.wireOp",EDGE,"E18.filletArc"),sQuery(id+"F0.wireOp",EDGE,"E19.filletArc"),sQuery(id+"F0.wireOp",EDGE,"E20.filletArc"),sQuery(id+"F0.wireOp",EDGE,"E25.0"),sQuery(id+"F0.wireOp",EDGE,"E25.1"),sQuery(id+"F0.wireOp",EDGE,"E25.2"),sQuery(id+"F0.wireOp",EDGE,"E25.3"),sQuery(id+"F0.wireOp",EDGE,"E25.4"),sQuery(id+"F0.wireOp",EDGE,"E25.5"),sQuery(id+"F0.wireOp",EDGE,"E25.6"),sQuery(id+"F0.wireOp",EDGE,"E25.7")])],"isStart":false});
            extrude(context, id + "F17", {"entities" : qUnion([Q0, Q1]), "endBound" : BoundingType.UP_TO_SURFACE, "depth" : 25 * mm, "endBoundEntityFace" : qUnion([Q2]), "offsetDistance" : 25 * mm});
        }
        {
            var Q0;
            Q0=makeQuery(id+"F17.opExtrude","SWEPT_BODY",BODY,{"disambiguationData":[OSD([sQuery(id+"F16.wireOp",EDGE,"E79.0"),sQuery(id+"F16.wireOp",EDGE,"E80.0"),sQuery(id+"F16.wireOp",EDGE,"E81.0"),sQuery(id+"F16.wireOp",EDGE,"E82.0"),sQuery(id+"F16.wireOp",EDGE,"E83.0"),sQuery(id+"F16.wireOp",EDGE,"E84.0"),sQuery(id+"F16.wireOp",EDGE,"E85.0"),sQuery(id+"F16.wireOp",EDGE,"E86.0"),sQuery(id+"F16.wireOp",EDGE,"E87.0"),sQuery(id+"F16.wireOp",EDGE,"E88.0"),sQuery(id+"F16.wireOp",EDGE,"E89.0"),sQuery(id+"F16.wireOp",EDGE,"E90.0"),sQuery(id+"F16.wireOp",EDGE,"E91.0"),sQuery(id+"F16.wireOp",EDGE,"E92.0"),sQuery(id+"F16.wireOp",EDGE,"E93.0"),sQuery(id+"F16.wireOp",EDGE,"E94.0"),sQuery(id+"F16.wireOp",EDGE,"E95.0"),sQuery(id+"F16.wireOp",EDGE,"E96.0"),sQuery(id+"F16.wireOp",EDGE,"E97.0"),sQuery(id+"F16.wireOp",EDGE,"E98.0"),sQuery(id+"F16.wireOp",EDGE,"E100"),sQuery(id+"F16.wireOp",EDGE,"E101"),sQuery(id+"F16.wireOp",EDGE,"E102"),sQuery(id+"F16.wireOp",EDGE,"E103"),sQuery(id+"F16.wireOp",EDGE,"E104"),sQuery(id+"F16.wireOp",EDGE,"E105"),sQuery(id+"F16.wireOp",EDGE,"E108.MirrorCS"),sQuery(id+"F16.wireOp",EDGE,"E109.MirrorCS"),sQuery(id+"F16.wireOp",EDGE,"E110.MirrorCS"),sQuery(id+"F16.wireOp",EDGE,"E111.MirrorC"),sQuery(id+"F16.wireOp",EDGE,"E112.MirrorCS"),sQuery(id+"F16.wireOp",EDGE,"E113.MirrorCS")])]});
            deleteBodies(context, id + "F18", {"entities" : qUnion([Q0])});
        }
    });
